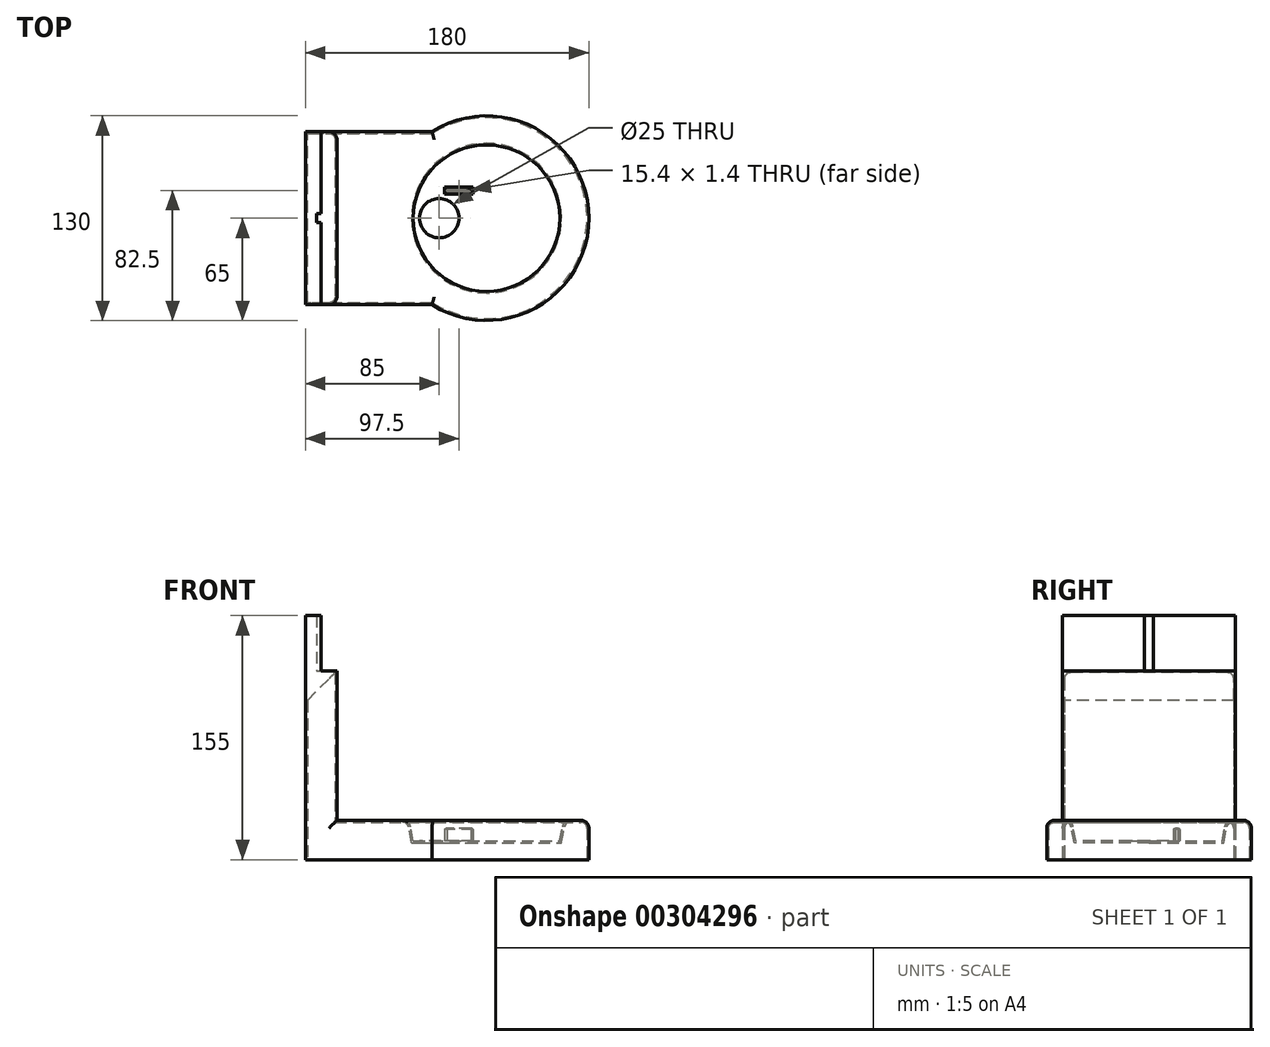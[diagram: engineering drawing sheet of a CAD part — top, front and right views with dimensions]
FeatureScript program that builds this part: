
annotation { "Feature Type Name" : "Feature", "Feature Type Description" : "" }
export const myFeature = defineFeature(function(context is Context, id is Id, definition is map)
    precondition{}
    {
        {
            var Q0;
            Q0=qCreatedBy(makeId("Top.planeOp"),FACE);
            var sketch = newSketch(context, id + "F0", { "sketchPlane" : qUnion([Q0])});
            skCircle(sketch, "E0", {"center": v(0, 0) * mm, "radius": 65 * mm});
            skLineSegment(sketch, "E1", {"start": v(0, 0) * mm, "end": v(0, 55) * mm});
            skLineSegment(sketch, "E2", {"start": v(0, 55) * mm, "end": v(-115, 55) * mm});
            skLineSegment(sketch, "E3", {"start": v(0, 0) * mm, "end": v(0, -55) * mm});
            skLineSegment(sketch, "E4", {"start": v(0, -55) * mm, "end": v(-115, -55) * mm});
            skLineSegment(sketch, "E5", {"start": v(-115, -55) * mm, "end": v(-115, 55) * mm});
            skLineSegment(sketch, "E6", {"start": v(-95, 55) * mm, "end": v(-95, -55) * mm});
            skSolve(sketch);
        }
        {
            var Q0;
            {var subQ1=sQuery(id+"F0.wireOp",EDGE,"E1");Q0=makeQuery(id+"F0.imprint","IMPRINT",FACE,{"disambiguationData":[TD([[makeQuery(id+"F0.imprint","IMPRINT",EDGE,{"derivedFrom":subQ1}),1.0]])]});}
            var Q1;
            {var subQ2=sQuery(id+"F0.wireOp",EDGE,"E1");Q1=makeQuery(id+"F0.imprint","IMPRINT",FACE,{"disambiguationData":[TD([[makeQuery(id+"F0.imprint","IMPRINT",EDGE,{"derivedFrom":subQ2}),-1.0]])]});}
            var Q2;
            {var subQ5=sQuery(id+"F0.wireOp",EDGE,"E6");Q2=makeQuery(id+"F0.imprint","IMPRINT",FACE,{"disambiguationData":[TD([[makeQuery(id+"F0.imprint","IMPRINT",EDGE,{"derivedFrom":subQ5}),1.0]])]});}
            extrude(context, id + "F1", {"entities" : qUnion([Q0, Q1, Q2]), "depth" : 25 * mm, "offsetDistance" : 25 * mm});
        }
        {
            var Q0;
            Q0=qCreatedBy(makeId("Front.planeOp"),FACE);
            var sketch = newSketch(context, id + "F2", { "sketchPlane" : qUnion([Q0])});
            skLineSegment(sketch, "E7", {"start": v(0, 30) * mm, "end": v(0, 12) * mm});
            skLineSegment(sketch, "E8", {"start": v(0, 12) * mm, "end": v(46.54, 12) * mm});
            skLineSegment(sketch, "E9", {"start": v(46.54, 12) * mm, "end": v(50, 30) * mm});
            skLineSegment(sketch, "E10", {"start": v(0, 30) * mm, "end": v(50, 30) * mm});
            skSolve(sketch);
        }
        {
            var Q0;
            Q0=qSketchRegion(id+"F2",true);
            var Q1;
            Q1=sQuery(id+"F2.wireOp",EDGE,"E7");
            revolve(context, id + "F3", {"operationType" : NewBodyOperationType.REMOVE, "entities" : qUnion([Q0]), "axis" : qUnion([Q1]), "revolveType" : RevolveType.FULL, "oppositeDirection" : true});
        }
        {
            var Q0;
            {var subQ0=sQuery(id+"F0.wireOp",EDGE,"E5");Q0=makeQuery(id+"F0.imprint","IMPRINT",FACE,{"disambiguationData":[TD([[makeQuery(id+"F0.imprint","IMPRINT",EDGE,{"derivedFrom":subQ0}),-1.0]])]});}
            extrude(context, id + "F4", {"entities" : qUnion([Q0]), "operationType" : NewBodyOperationType.ADD, "depth" : 120 * mm, "offsetDistance" : 25 * mm});
        }
        {
            var Q0;
            Q0=makeQuery(id+"F3.boolean.opBoolean","COPY",FACE,{"derivedFrom":makeQuery(id+"F3.opRevolve","SWEPT_FACE",FACE,{"disambiguationData":[OSD([sQuery(id+"F2.wireOp",EDGE,"E8")])]})});
            var sketch = newSketch(context, id + "F5", { "sketchPlane" : qUnion([Q0])});
            skCircle(sketch, "E11", {"center": v(-30, 0) * mm, "radius": 12.5 * mm});
            skCircle(sketch, "E12", {"center": v(-30, 0) * mm, "radius": 13.3 * mm});
            skSolve(sketch);
        }
        {
            var Q0;
            Q0=makeQuery(id+"F4.opExtrude","CAP_FACE",FACE,{"disambiguationData":[OSD([sQuery(id+"F0.wireOp",EDGE,"E2"),sQuery(id+"F0.wireOp",EDGE,"E4"),sQuery(id+"F0.wireOp",EDGE,"E5"),sQuery(id+"F0.wireOp",EDGE,"E6")])],"isStart":false});
            var sketch = newSketch(context, id + "F6", { "sketchPlane" : qUnion([Q0])});
            skCircle(sketch, "E13", {"center": v(-105, 0) * mm, "radius": 2.8 * mm});
            skLineSegment(sketch, "E14", {"start": v(-105, 0) * mm, "end": v(-105, 2.8) * mm});
            skLineSegment(sketch, "E15", {"start": v(-105, 2.8) * mm, "end": v(-107.8, 2.8) * mm});
            skLineSegment(sketch, "E16", {"start": v(-107.8, 2.8) * mm, "end": v(-107.8, 0) * mm});
            skLineSegment(sketch, "E17", {"start": v(-107.8, 0) * mm, "end": v(-107.8, -2.8) * mm});
            skLineSegment(sketch, "E18", {"start": v(-107.8, -2.8) * mm, "end": v(-105, -2.8) * mm});
            skLineSegment(sketch, "E19", {"start": v(-105, -2.8) * mm, "end": v(-105, 0) * mm});
            skSolve(sketch);
        }
        {
            var Q0;
            Q0=qCreatedBy(makeId("Front.planeOp"),FACE);
            var sketch = newSketch(context, id + "F7", { "sketchPlane" : qUnion([Q0])});
            skLineSegment(sketch, "E20", {"start": v(-30, 12) * mm, "end": v(-30, 9.78) * mm});
            skLineSegment(sketch, "E21", {"start": v(-37.54, 2.8) * mm, "end": v(-64.38, 2.8) * mm});
            skArc(sketch, "E22", {"start": v(-37.54, 2.8) * mm, "mid": v(-32.25, 4.64) * mm, "end": v(-30, 9.78) * mm});
            skLineSegment(sketch, "E23", {"start": v(-64.38, 2.8) * mm, "end": v(-98, 2.8) * mm});
            skLineSegment(sketch, "E24", {"start": v(-105, 120) * mm, "end": v(-105, 9.8) * mm});
            skArc(sketch, "E25", {"start": v(-105, 9.8) * mm, "mid": v(-102.95, 4.85) * mm, "end": v(-98, 2.8) * mm});
            skSolve(sketch);
        }
        {
            var Q0;
            Q0=makeQuery(id+"F1.opExtrude","CAP_EDGE",EDGE,{"disambiguationData":[OSD([sQuery(id+"F0.wireOp",EDGE,"E4")])],"isStart":false});
            var Q1;
            Q1=makeQuery(id+"F1.opExtrude","CAP_EDGE",EDGE,{"disambiguationData":[OSD([sQuery(id+"F0.wireOp",EDGE,"E0")])],"isStart":false});
            var Q2;
            Q2=makeQuery(id+"F1.opExtrude","CAP_EDGE",EDGE,{"disambiguationData":[OSD([sQuery(id+"F0.wireOp",EDGE,"E2")])],"isStart":false});
            var Q3;
            Q3=makeQuery(id+"F1.opExtrude","CAP_EDGE",EDGE,{"disambiguationData":[OSD([sQuery(id+"F0.wireOp",EDGE,"E6")])],"isStart":false});
            var Q4;
            Q4=makeQuery(id+"F4.opExtrude","SWEPT_EDGE",EDGE,{"disambiguationData":[OSD([sQuery(id+"F0.wireOp",EDGE,"E4"),sQuery(id+"F0.wireOp",EDGE,"E6")])]});
            var Q5;
            Q5=makeQuery(id+"F4.opExtrude","SWEPT_EDGE",EDGE,{"disambiguationData":[OSD([sQuery(id+"F0.wireOp",EDGE,"E2"),sQuery(id+"F0.wireOp",EDGE,"E6")])]});
            var Q6;
            Q6=makeQuery(id+"F3.boolean.opBoolean","INTERSECT",EDGE,{"derivedFrom":[makeQuery(id+"F1.opExtrude","CAP_FACE",FACE,{"disambiguationData":[OSD([sQuery(id+"F0.wireOp",EDGE,"E0"),sQuery(id+"F0.wireOp",EDGE,"E2"),sQuery(id+"F0.wireOp",EDGE,"E4"),sQuery(id+"F0.wireOp",EDGE,"E6")])],"isStart":false}),makeQuery(id+"F3.opRevolve","SWEPT_FACE",FACE,{"disambiguationData":[OSD([sQuery(id+"F2.wireOp",EDGE,"E9")])]})]});
            fillet(context, id + "F8", {"entities" : qUnion([Q0, Q1, Q2, Q3, Q4, Q5, Q6]), "radius" : 5 * mm, "tangentPropagation" : true, "allowEdgeOverflow" : false});
        }
        {
            var Q0;
            {var subQ0=sQuery(id+"F0.wireOp",EDGE,"E6");var subQ1=sQuery(id+"F0.wireOp",EDGE,"E4");var subQ2=sQuery(id+"F0.wireOp",EDGE,"E2");Q0=makeQuery(id+"F4.boolean.opBoolean","MERGE",FACE,{"derivedFrom":[makeQuery(id+"F1.opExtrude","CAP_FACE",FACE,{"disambiguationData":[OSD([sQuery(id+"F0.wireOp",EDGE,"E0"),subQ2,subQ1,subQ0])],"isStart":true}),makeQuery(id+"F4.opExtrude","CAP_FACE",FACE,{"disambiguationData":[OSD([subQ2,subQ1,sQuery(id+"F0.wireOp",EDGE,"E5"),subQ0])],"isStart":true})]});}
            shell(context, id + "F9", {"entities" : qUnion([Q0]), "thickness" : 1.2 * mm});
        }
        {
            var Q0;
            {var subQ0=sQuery(id+"F0.wireOp",EDGE,"E5");Q0=makeQuery(id+"F9.opShell","OFFSET_EDGE",EDGE,{"disambiguationData":[OSD([subQ0]),TDD([makeQuery(id+"F4.opExtrude","CAP_EDGE",EDGE,{"disambiguationData":[OSD([subQ0])],"isStart":false})])]});}
            chamfer(context, id + "F10", {"entities" : qUnion([Q0]), "width" : 17.6 * mm, "tangentPropagation" : true});
        }
        {
            var Q0;
            Q0=makeQuery(id+"F5.imprint","IMPRINT",FACE,{"disambiguationData":[TD([[makeQuery(id+"F5.imprint","IMPRINT",EDGE,{"derivedFrom":sQuery(id+"F5.wireOp",EDGE,"E11")}),1.0]])]});
            var Q1;
            Q1=sQuery(id+"F5.wireOp",EDGE,"E11");
            extrude(context, id + "F11", {"entities" : qUnion([Q0]), "operationType" : NewBodyOperationType.REMOVE, "surfaceEntities" : qUnion([Q1]), "oppositeDirection" : true, "depth" : 25 * mm, "offsetDistance" : 25 * mm});
        }
        {
            var Q0;
            {var subQ0=sQuery(id+"F6.wireOp",EDGE,"E15");Q0=makeQuery(id+"F6.imprint","IMPRINT",FACE,{"disambiguationData":[TD([[makeQuery(id+"F6.imprint","IMPRINT",EDGE,{"derivedFrom":subQ0}),-1.0]])]});}
            var sketch = newSketch(context, id + "F12", { "sketchPlane" : qUnion([Q0])});
            skLineSegment(sketch, "E26.bottom", {"start": v(-95, -55) * mm, "end": v(-115, -55) * mm});
            skLineSegment(sketch, "E26.top", {"start": v(-95, 55) * mm, "end": v(-115, 55) * mm});
            skLineSegment(sketch, "E26.left", {"start": v(-95, -55) * mm, "end": v(-95, 55) * mm});
            skLineSegment(sketch, "E26.right", {"start": v(-115, -55) * mm, "end": v(-115, 55) * mm});
            skPoint(sketch, "E26.middle", {"position": v(-105, 0) * mm});
            skLineSegment(sketch, "E27", {"start": v(-105, 0) * mm, "end": v(-105, 55) * mm});
            skLineSegment(sketch, "E28", {"start": v(-105, 0) * mm, "end": v(-105, -55) * mm});
            skSolve(sketch);
        }
        {
            var Q0;
            {var subQ8=sQuery(id+"F12.wireOp",EDGE,"E26.right");Q0=makeQuery(id+"F12.imprint","IMPRINT",FACE,{"disambiguationData":[TD([[makeQuery(id+"F12.imprint","IMPRINT",EDGE,{"derivedFrom":subQ8}),-1.0]])]});}
            extrude(context, id + "F13", {"entities" : qUnion([Q0]), "operationType" : NewBodyOperationType.ADD, "depth" : 35 * mm, "offsetDistance" : 25 * mm});
        }
        {
            var Q0;
            Q0=makeQuery(id+"F5.imprint","IMPRINT",FACE,{"disambiguationData":[TD([[makeQuery(id+"F5.imprint","IMPRINT",EDGE,{"derivedFrom":sQuery(id+"F5.wireOp",EDGE,"E12")}),-1.0]])]});
            var sketch = newSketch(context, id + "F14", { "sketchPlane" : qUnion([Q0])});
            skLineSegment(sketch, "E29.bottom", {"start": v(-8.4, 15.4) * mm, "end": v(-26.6, 15.4) * mm});
            skLineSegment(sketch, "E29.top", {"start": v(-8.4, 19.6) * mm, "end": v(-26.6, 19.6) * mm});
            skLineSegment(sketch, "E29.left", {"start": v(-8.4, 15.4) * mm, "end": v(-8.4, 19.6) * mm});
            skLineSegment(sketch, "E29.right", {"start": v(-26.6, 15.4) * mm, "end": v(-26.6, 19.6) * mm});
            skPoint(sketch, "E29.middle", {"position": v(-17.5, 17.5) * mm});
            skLineSegment(sketch, "E30.bottom", {"start": v(-9.8, 18.2) * mm, "end": v(-25.2, 18.2) * mm});
            skLineSegment(sketch, "E30.top", {"start": v(-9.8, 16.8) * mm, "end": v(-25.2, 16.8) * mm});
            skLineSegment(sketch, "E30.left", {"start": v(-9.8, 18.2) * mm, "end": v(-9.8, 16.8) * mm});
            skLineSegment(sketch, "E30.right", {"start": v(-25.2, 18.2) * mm, "end": v(-25.2, 16.8) * mm});
            skSolve(sketch);
        }
        {
            var Q0;
            Q0=makeQuery(id+"F14.imprint","IMPRINT",FACE,{"disambiguationData":[TD([[makeQuery(id+"F14.imprint","IMPRINT",EDGE,{"derivedFrom":sQuery(id+"F14.wireOp",EDGE,"E29.bottom")}),-1.0]])]});
            extrude(context, id + "F15", {"entities" : qUnion([Q0]), "operationType" : NewBodyOperationType.ADD, "depth" : 8 * mm, "offsetDistance" : 25 * mm});
        }
        {
            var Q0;
            Q0=makeQuery(id+"F15.opExtrude","CAP_EDGE",EDGE,{"disambiguationData":[OSD([sQuery(id+"F14.wireOp",EDGE,"E29.bottom")])],"isStart":false});
            var Q1;
            Q1=makeQuery(id+"F15.opExtrude","CAP_EDGE",EDGE,{"disambiguationData":[OSD([sQuery(id+"F14.wireOp",EDGE,"E29.left")])],"isStart":false});
            var Q2;
            Q2=makeQuery(id+"F15.opExtrude","CAP_EDGE",EDGE,{"disambiguationData":[OSD([sQuery(id+"F14.wireOp",EDGE,"E29.top")])],"isStart":false});
            var Q3;
            Q3=makeQuery(id+"F15.opExtrude","CAP_EDGE",EDGE,{"disambiguationData":[OSD([sQuery(id+"F14.wireOp",EDGE,"E29.right")])],"isStart":false});
            chamfer(context, id + "F16", {"entities" : qUnion([Q0, Q1, Q2, Q3]), "width" : 0.8 * mm, "tangentPropagation" : true});
        }
        {
            var Q0;
            Q0=makeQuery(id+"F14.imprint","IMPRINT",FACE,{"disambiguationData":[TD([[makeQuery(id+"F14.imprint","IMPRINT",EDGE,{"derivedFrom":sQuery(id+"F14.wireOp",EDGE,"E30.bottom")}),1.0]])]});
            extrude(context, id + "F17", {"entities" : qUnion([Q0]), "operationType" : NewBodyOperationType.REMOVE, "oppositeDirection" : true, "depth" : 25 * mm, "offsetDistance" : 25 * mm});
        }
    });
